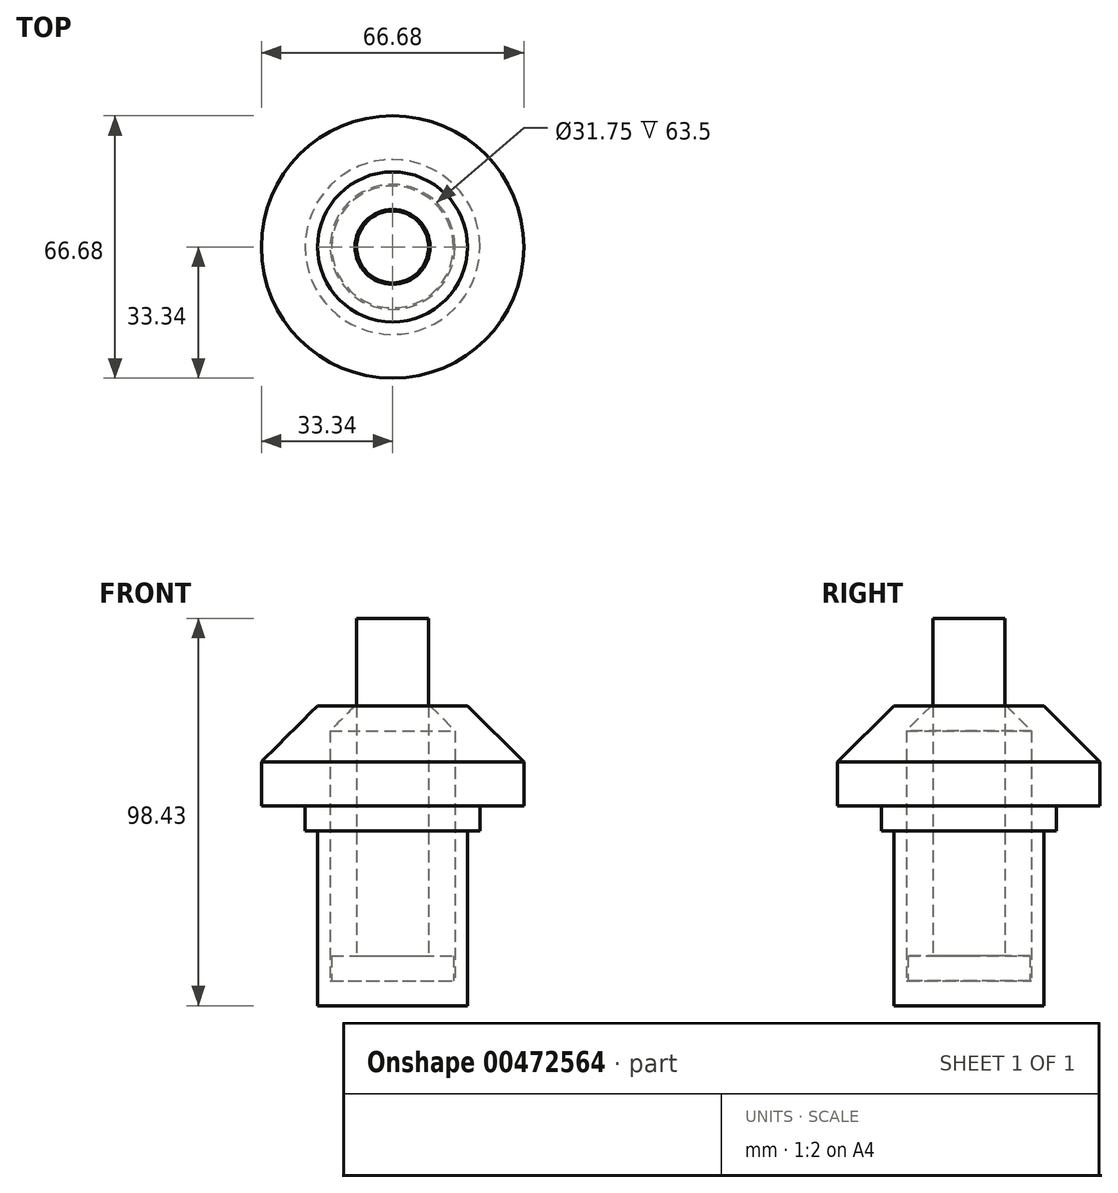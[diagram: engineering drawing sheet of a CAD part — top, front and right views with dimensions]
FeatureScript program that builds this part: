
annotation { "Feature Type Name" : "Feature", "Feature Type Description" : "" }
export const myFeature = defineFeature(function(context is Context, id is Id, definition is map)
    precondition{}
    {
        {
            var Q0;
            Q0=qCreatedBy(makeId("Front.planeOp"),FACE);
            var sketch = newSketch(context, id + "F0", { "sketchPlane" : qUnion([Q0])});
            skLineSegment(sketch, "E0", {"start": v(0, 0) * mm, "end": v(0, 98.42) * mm});
            skLineSegment(sketch, "E1", {"start": v(0, 76.2) * mm, "end": v(19.05, 76.2) * mm});
            skLineSegment(sketch, "E2", {"start": v(19.05, 76.2) * mm, "end": v(33.34, 61.91) * mm});
            skLineSegment(sketch, "E3", {"start": v(33.34, 61.91) * mm, "end": v(33.34, 50.8) * mm});
            skLineSegment(sketch, "E4", {"start": v(33.34, 50.8) * mm, "end": v(22.23, 50.8) * mm});
            skLineSegment(sketch, "E5", {"start": v(22.23, 50.8) * mm, "end": v(22.23, 44.45) * mm});
            skLineSegment(sketch, "E6", {"start": v(22.23, 44.45) * mm, "end": v(19.05, 44.45) * mm});
            skLineSegment(sketch, "E7", {"start": v(19.05, 44.45) * mm, "end": v(19.05, 0) * mm});
            skLineSegment(sketch, "E8", {"start": v(19.05, 0) * mm, "end": v(0, 0) * mm});
            skLineSegment(sketch, "E9", {"start": v(0, 98.42) * mm, "end": v(0, 104.44) * mm, "construction": true});
            skLineSegment(sketch, "E10", {"start": v(0, 98.42) * mm, "end": v(9.13, 98.42) * mm});
            skLineSegment(sketch, "E11", {"start": v(9.13, 98.42) * mm, "end": v(9.13, 12.7) * mm});
            skLineSegment(sketch, "E12", {"start": v(0, 6.35) * mm, "end": v(15.88, 6.35) * mm});
            skLineSegment(sketch, "E13", {"start": v(15.88, 6.35) * mm, "end": v(15.88, 69.85) * mm});
            skLineSegment(sketch, "E14", {"start": v(9.13, 12.7) * mm, "end": v(15.48, 12.7) * mm});
            skLineSegment(sketch, "E15", {"start": v(15.48, 12.7) * mm, "end": v(15.48, 6.35) * mm});
            skLineSegment(sketch, "E16", {"start": v(15.88, 69.85) * mm, "end": v(9.53, 76.2) * mm});
            skSolve(sketch);
        }
        {
            var Q0;
            {var subQ5=sQuery(id+"F0.wireOp",EDGE,"E2");Q0=makeQuery(id+"F0.imprint","IMPRINT",FACE,{"disambiguationData":[TD([[makeQuery(id+"F0.imprint","IMPRINT",EDGE,{"derivedFrom":subQ5}),-1.0]])]});}
            var Q1;
            Q1=sQuery(id+"F0.wireOp",EDGE,"E9");
            revolve(context, id + "F1", {"surfaceOperationType" : NewSurfaceOperationType.NEW, "entities" : qUnion([Q0]), "axis" : qUnion([Q1]), "revolveType" : RevolveType.FULL});
        }
        {
            var Q0;
            {var subQ0=sQuery(id+"F0.wireOp",EDGE,"E10");Q0=makeQuery(id+"F0.imprint","IMPRINT",FACE,{"disambiguationData":[TD([[makeQuery(id+"F0.imprint","IMPRINT",EDGE,{"derivedFrom":subQ0}),-1.0]])]});}
            var Q1;
            {var subQ0=sQuery(id+"F0.wireOp",EDGE,"E14");Q1=makeQuery(id+"F0.imprint","IMPRINT",FACE,{"disambiguationData":[TD([[makeQuery(id+"F0.imprint","IMPRINT",EDGE,{"derivedFrom":subQ0}),-1.0]])]});}
            var Q2;
            Q2=sQuery(id+"F0.wireOp",EDGE,"E9");
            revolve(context, id + "F2", {"surfaceOperationType" : NewSurfaceOperationType.NEW, "entities" : qUnion([Q0, Q1]), "axis" : qUnion([Q2]), "revolveType" : RevolveType.FULL});
        }
    });
